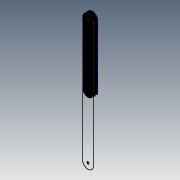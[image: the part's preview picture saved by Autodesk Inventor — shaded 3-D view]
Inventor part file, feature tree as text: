
AUTODESK INVENTOR PART (.ipt)
format: ipt  version: 2015 (Build 190159000, 159)  size: 92,160 bytes
history: native  units: mm
features: other x5, sketch x2, reference x2, extrude x1
ambient origin geometry x8: Origin, YZ Plane, XZ Plane, XY Plane, X Axis, Y Axis, Z Axis, Center Point
bodies: Solid1 (feature_tree)
feature tree (10):
  other  "Blocks"
  extrude  "Extrusion1"  Depth=50.0mm
  sketch  "Sketch2"  dims[d2=10.0mm d3=10.0mm d4=20.0mm d5=0.0mm d6=285.0mm]
  other  "DXF"
  sketch  "Sketch1"  dims[d0=50.0mm d1=50.0mm]
  reference  "Reference1"
  reference  "Reference2"
  other  "Block1"
  other  "Block1:1"
  other  "Block1:2"
